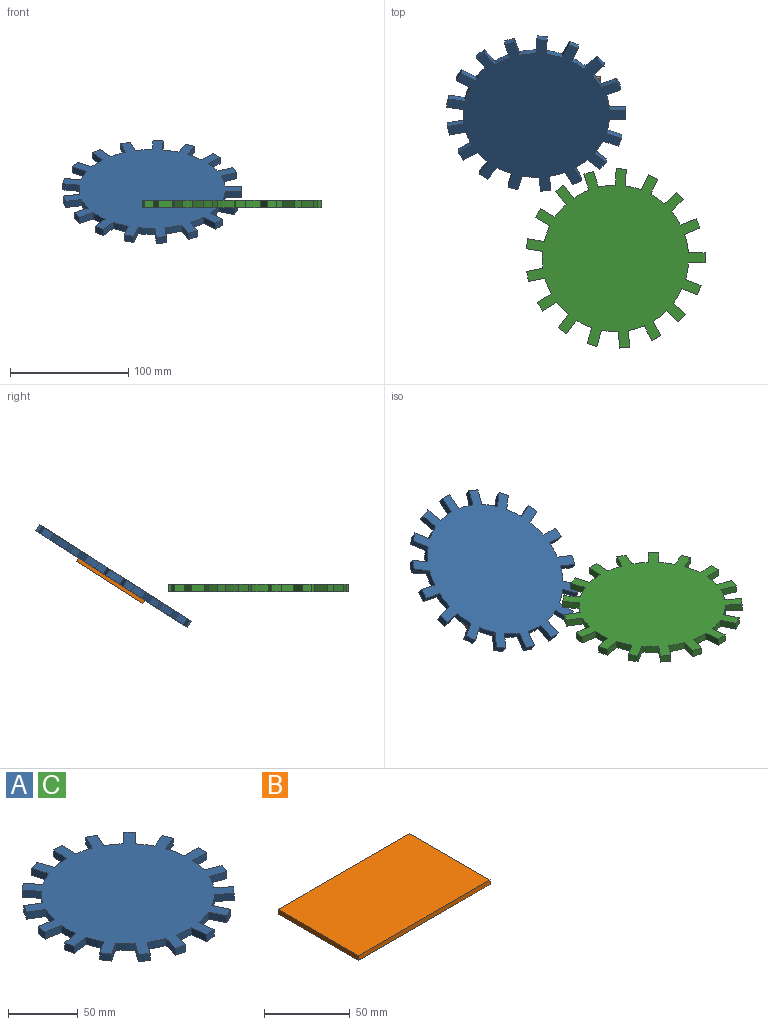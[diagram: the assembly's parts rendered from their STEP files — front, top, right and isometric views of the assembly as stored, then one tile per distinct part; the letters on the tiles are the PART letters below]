
ASSEMBLY  parts=3 mates=1
PART A: 70 faces, bbox 151x151.5x6.1 mm
  f0: plane 12.96x6.1mm, normal (-0.38,0.92,0), area 85.6mm2, adj f1,f67,f68,f69
  f1: cylinder r=61.81mm len=11.82mm, axis (0,0,-1), area 86.7mm2, adj f0,f2,f68,f69
  f2: plane 10.1x9.66mm, normal (0.69,-0.72,0), area 85.2mm2, adj f1,f3,f68,f69
  f3: plane 6.16x6.1mm, normal (0.72,0.69,0), area 51.9mm2, adj f2,f4,f68,f69
  f4: plane 10.15x9.7mm, normal (-0.69,0.72,0), area 85.6mm2, adj f3,f5,f68,f69
  f5: cylinder r=61.81mm len=11.58mm, axis (0,0,-1), area 86.7mm2, adj f4,f6,f68,f69
  f6: plane 12.65x6.1mm, normal (0.9,-0.43,0), area 85.2mm2, adj f5,f7,f68,f69
  f7: plane 7.71x6.1mm, normal (0.43,0.9,0), area 51.9mm2, adj f6,f8,f68,f69
  f8: plane 12.7x6.1mm, normal (-0.9,0.43,0), area 85.6mm2, adj f7,f9,f68,f69
  f9: cylinder r=61.81mm len=13.75mm, axis (0,0,-1), area 86.7mm2, adj f8,f10,f68,f69
  f10: plane 13.94x6.1mm, normal (1,-0.07,0), area 85.2mm2, adj f9,f11,f68,f69
  f11: plane 8.5x6.1mm, normal (0.07,1,0), area 51.9mm2, adj f10,f12,f68,f69
  f12: plane 14x6.1mm, normal (-1,0.07,0), area 85.6mm2, adj f11,f13,f68,f69
  f13: cylinder r=61.81mm len=14.09mm, axis (0,0,-1), area 86.7mm2, adj f12,f14,f68,f69
  f14: plane 13.37x6.1mm, normal (0.96,0.29,0), area 85.2mm2, adj f13,f15,f68,f69
  f15: plane 8.15x6.1mm, normal (-0.29,0.96,0), area 51.9mm2, adj f14,f16,f68,f69
  f16: plane 13.43x6.1mm, normal (-0.96,-0.29,0), area 85.6mm2, adj f15,f17,f68,f69
  f17: cylinder r=61.81mm len=12.54mm, axis (0,0,-1), area 86.7mm2, adj f16,f18,f68,f69
  f18: plane 11x8.62mm, normal (0.79,0.62,0), area 85.2mm2, adj f17,f19,f68,f69
  f19: plane 6.71x6.1mm, normal (-0.62,0.79,0), area 51.9mm2, adj f18,f20,f68,f69
  f20: plane 11.05x8.65mm, normal (-0.79,-0.62,0), area 85.6mm2, adj f19,f21,f68,f69
  f21: cylinder r=61.81mm len=10.71mm, axis (0,0,-1), area 86.7mm2, adj f20,f22,f68,f69
  f22: plane 12x7.17mm, normal (0.51,0.86,0), area 85.2mm2, adj f21,f23,f68,f69
  f23: plane 7.31x6.1mm, normal (-0.86,0.51,0), area 51.9mm2, adj f22,f24,f68,f69
  f24: plane 12.05x7.2mm, normal (-0.51,-0.86,0), area 85.6mm2, adj f23,f25,f68,f69
  f25: cylinder r=61.81mm len=13.34mm, axis (0,0,-1), area 86.7mm2, adj f24,f26,f68,f69
  f26: plane 13.77x6.1mm, normal (0.17,0.99,0), area 85.2mm2, adj f25,f27,f68,f69
  f27: plane 8.4x6.1mm, normal (-0.99,0.17,0), area 51.9mm2, adj f26,f28,f68,f69
  f28: plane 13.83x6.1mm, normal (-0.17,-0.99,0), area 85.6mm2, adj f27,f29,f68,f69
  f29: cylinder r=61.81mm len=14.19mm, axis (0,0,-1), area 86.7mm2, adj f28,f30,f68,f69
  f30: plane 13.7x6.1mm, normal (-0.2,0.98,0), area 85.2mm2, adj f29,f31,f68,f69
  f31: plane 8.36x6.1mm, normal (-0.98,-0.2,0), area 51.9mm2, adj f30,f32,f68,f69
  f32: plane 13.76x6.1mm, normal (0.2,-0.98,0), area 85.6mm2, adj f31,f33,f68,f69
  f33: cylinder r=61.81mm len=13.13mm, axis (0,0,-1), area 86.7mm2, adj f32,f34,f68,f69
  f34: plane 11.8x7.49mm, normal (-0.54,0.84,0), area 85.2mm2, adj f33,f35,f68,f69
  f35: plane 7.19x6.1mm, normal (-0.84,-0.54,0), area 51.9mm2, adj f34,f36,f68,f69
  f36: plane 11.85x7.52mm, normal (0.54,-0.84,0), area 85.6mm2, adj f35,f37,f68,f69
  f37: cylinder r=61.81mm len=10.32mm, axis (0,0,-1), area 86.7mm2, adj f36,f38,f68,f69
  f38: plane 11.23x8.32mm, normal (-0.8,0.6,0), area 85.2mm2, adj f37,f39,f68,f69
  f39: plane 6.85x6.1mm, normal (-0.6,-0.8,0), area 51.9mm2, adj f38,f40,f68,f69
  f40: plane 11.28x8.35mm, normal (0.8,-0.6,0), area 85.6mm2, adj f39,f41,f68,f69
  f41: cylinder r=61.81mm len=12.8mm, axis (0,0,-1), area 86.7mm2, adj f40,f42,f68,f69
  f42: plane 13.47x6.1mm, normal (-0.96,0.27,0), area 85.2mm2, adj f41,f43,f68,f69
  f43: plane 8.21x6.1mm, normal (-0.27,-0.96,0), area 51.9mm2, adj f42,f44,f68,f69
  f44: plane 13.53x6.1mm, normal (0.96,-0.27,0), area 85.6mm2, adj f43,f45,f68,f69
  f45: cylinder r=61.81mm len=14.15mm, axis (0,0,-1), area 86.7mm2, adj f44,f46,f68,f69
  f46: plane 13.91x6.1mm, normal (-1,-0.1,0), area 85.2mm2, adj f45,f47,f68,f69
  f47: plane 8.48x6.1mm, normal (0.1,-1,0), area 51.9mm2, adj f46,f48,f68,f69
  f48: plane 13.97x6.1mm, normal (1,0.1,0), area 85.6mm2, adj f47,f49,f68,f69
  f49: cylinder r=61.81mm len=13.6mm, axis (0,0,-1), area 86.7mm2, adj f48,f50,f68,f69
  f50: plane 12.48x6.29mm, normal (-0.89,-0.45,0), area 85.2mm2, adj f49,f51,f68,f69
  f51: plane 7.61x6.1mm, normal (0.45,-0.89,0), area 51.9mm2, adj f50,f52,f68,f69
  f52: plane 12.54x6.32mm, normal (0.89,0.45,0), area 85.6mm2, adj f51,f53,f68,f69
  f53: cylinder r=61.81mm len=11.23mm, axis (0,0,-1), area 86.7mm2, adj f52,f54,f68,f69
  f54: plane 10.36x9.38mm, normal (-0.67,-0.74,0), area 85.2mm2, adj f53,f55,f68,f69
  f55: plane 6.32x6.1mm, normal (0.74,-0.67,0), area 51.9mm2, adj f54,f56,f68,f69
  f56: plane 10.4x9.42mm, normal (0.67,0.74,0), area 85.6mm2, adj f55,f57,f68,f69
  f57: cylinder r=61.81mm len=12.13mm, axis (0,0,-1), area 86.7mm2, adj f56,f58,f68,f69
  f58: plane 13.04x6.1mm, normal (-0.36,-0.93,0), area 85.2mm2, adj f57,f59,f68,f69
  f59: plane 7.95x6.1mm, normal (0.93,-0.36,0), area 51.9mm2, adj f58,f60,f68,f69
  f60: plane 13.1x6.1mm, normal (0.36,0.93,0), area 85.6mm2, adj f59,f61,f68,f69
  f61: cylinder r=61.81mm len=13.97mm, axis (0,0,-1), area 86.7mm2, adj f60,f62,f68,f69
  f62: plane 13.98x6.1mm, normal (0,-1,0), area 85.2mm2, adj f61,f63,f68,f69
  f63: plane 8.52x6.1mm, normal (1,0,0), area 51.9mm2, adj f62,f64,f68,f69
  f64: plane 14.04x6.1mm, normal (0,1,0), area 85.6mm2, adj f63,f65,f68,f69
  f65: cylinder r=61.81mm len=15.51mm, axis (0,0,-1), area 96.8mm2, adj f64,f66,f68,f69
  f66: plane 12.9x6.1mm, normal (0.38,-0.92,0), area 85.2mm2, adj f65,f67,f68,f69
  f67: plane 7.86x6.1mm, normal (0.92,0.38,0), area 51.9mm2, adj f0,f66,f68,f69
  f68: plane 151.49x151.04mm, normal (0,0,1), area 14018.7mm2, adj f0,f1,f2,f3,f4,f5,f6,f7
  f69: plane 151.49x151.04mm, normal (0,0,-1), area 14018.7mm2, adj f0,f1,f2,f3,f4,f5,f6,f7
PART B: 6 faces, bbox 108.3x66.3x3.3 mm
  f0: plane 108.27x3.3mm, normal (0,1,0), area 357.5mm2, adj f1,f3,f4,f5
  f1: plane 66.34x3.3mm, normal (-1,0,0), area 219.1mm2, adj f0,f2,f4,f5
  f2: plane 108.27x3.3mm, normal (0,-1,0), area 357.5mm2, adj f1,f3,f4,f5
  f3: plane 66.34x3.3mm, normal (1,0,0), area 219.1mm2, adj f0,f2,f4,f5
  f4: plane 108.27x66.34mm, normal (0,0,1), area 7183.1mm2, adj f0,f1,f2,f3
  f5: plane 108.27x66.34mm, normal (0,0,-1), area 7183.1mm2, adj f0,f1,f2,f3
PART C: same geometry as A
PLACE A rot(axis=(1,0,0),32.6deg) t=(-23.27,67.69,48.71)mm
PLACE B rot(axis=(1,0,0),32.6deg) t=(-25.53,74.61,49.21)mm
PLACE C t=(43.57,-56.16,38.08)mm
MATE revolute B.f4 <-> A.f1  axis (0,-0.54,0.84) through (-23.27,67.69,48.71)mm
